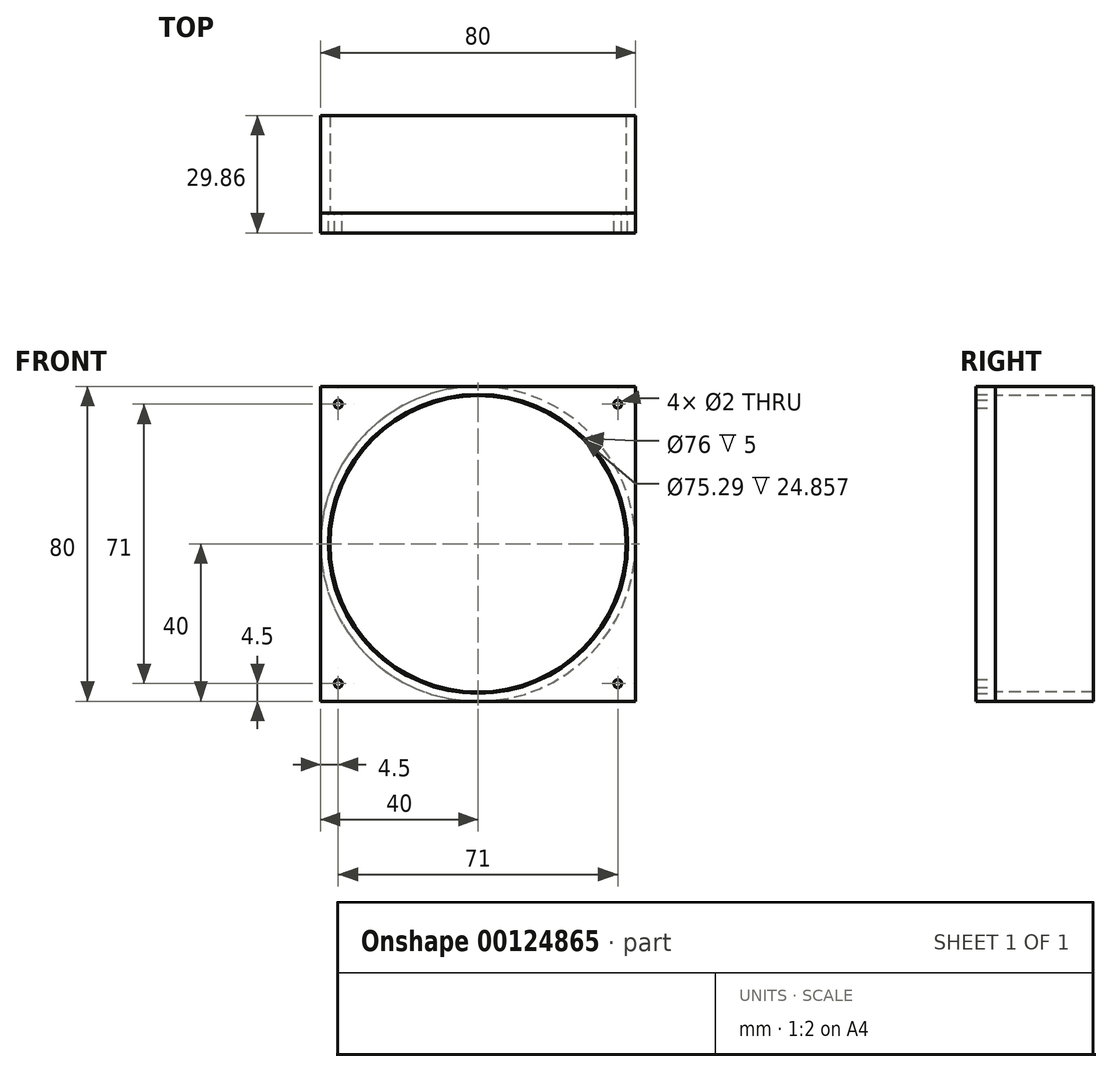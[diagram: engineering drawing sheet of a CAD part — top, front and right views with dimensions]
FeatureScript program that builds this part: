
annotation { "Feature Type Name" : "Feature", "Feature Type Description" : "" }
export const myFeature = defineFeature(function(context is Context, id is Id, definition is map)
    precondition{}
    {
        {
            var Q0;
            Q0=qCreatedBy(makeId("Front.planeOp"),FACE);
            var sketch = newSketch(context, id + "F0", { "sketchPlane" : qUnion([Q0])});
            skLineSegment(sketch, "E0.bottom", {"start": v(40, -40) * mm, "end": v(-40, -40) * mm});
            skLineSegment(sketch, "E0.top", {"start": v(40, 40) * mm, "end": v(-40, 40) * mm});
            skLineSegment(sketch, "E0.left", {"start": v(40, -40) * mm, "end": v(40, 40) * mm});
            skLineSegment(sketch, "E0.right", {"start": v(-40, -40) * mm, "end": v(-40, 40) * mm});
            skPoint(sketch, "E0.middle", {"position": v(0, 0) * mm});
            skCircle(sketch, "E1", {"center": v(-35.5, 35.5) * mm, "radius": 1 * mm});
            skCircle(sketch, "E2", {"center": v(35.5, 35.5) * mm, "radius": 1 * mm});
            skCircle(sketch, "E3", {"center": v(35.5, -35.5) * mm, "radius": 1 * mm});
            skCircle(sketch, "E4", {"center": v(-35.5, -35.5) * mm, "radius": 1 * mm});
            skCircle(sketch, "E5", {"center": v(0, 0) * mm, "radius": 38 * mm});
            skPoint(sketch, "E6.endSnap0", {"position": v(-40, 0) * mm});
            skSolve(sketch);
        }
        {
            var Q0;
            Q0=makeQuery(id+"F0.imprint","IMPRINT",FACE,{"disambiguationData":[TD([[makeQuery(id+"F0.imprint","IMPRINT",EDGE,{"derivedFrom":sQuery(id+"F0.wireOp",EDGE,"E0.bottom")}),-1.0]])]});
            extrude(context, id + "F1", {"entities" : qUnion([Q0]), "depth" : 5 * mm, "symmetric" : true});
        }
        {
            var Q0;
            Q0=makeQuery(id+"F1.opExtrude","CAP_FACE",FACE,{"disambiguationData":[OSD([sQuery(id+"F0.wireOp",EDGE,"E0.bottom"),sQuery(id+"F0.wireOp",EDGE,"E0.top"),sQuery(id+"F0.wireOp",EDGE,"E0.left"),sQuery(id+"F0.wireOp",EDGE,"E0.right"),sQuery(id+"F0.wireOp",EDGE,"E1"),sQuery(id+"F0.wireOp",EDGE,"E2"),sQuery(id+"F0.wireOp",EDGE,"E3"),sQuery(id+"F0.wireOp",EDGE,"E4"),sQuery(id+"F0.wireOp",EDGE,"E5")])],"isStart":true});
            var sketch = newSketch(context, id + "F3", { "sketchPlane" : qUnion([Q0])});
            skCircle(sketch, "E7", {"center": v(0, 0) * mm, "radius": 37.64 * mm});
            skCircle(sketch, "E8", {"center": v(0, 0) * mm, "radius": 40 * mm});
            skSolve(sketch);
        }
        {
            var Q0;
            Q0=qSketchRegion(id+"F3",true);
            var Q1;
            Q1=makeQuery(id+"F1.opExtrude","SWEPT_BODY",BODY,{"disambiguationData":[OSD([sQuery(id+"F0.wireOp",EDGE,"E0.bottom"),sQuery(id+"F0.wireOp",EDGE,"E0.top"),sQuery(id+"F0.wireOp",EDGE,"E0.left"),sQuery(id+"F0.wireOp",EDGE,"E0.right"),sQuery(id+"F0.wireOp",EDGE,"E1"),sQuery(id+"F0.wireOp",EDGE,"E2"),sQuery(id+"F0.wireOp",EDGE,"E3"),sQuery(id+"F0.wireOp",EDGE,"E4"),sQuery(id+"F0.wireOp",EDGE,"E5")])]});
            extrude(context, id + "F4", {"entities" : qUnion([Q0]), "operationType" : NewBodyOperationType.ADD, "endBoundEntityBody" : qUnion([Q1]), "depth" : 24.86 * mm});
        }
    });
